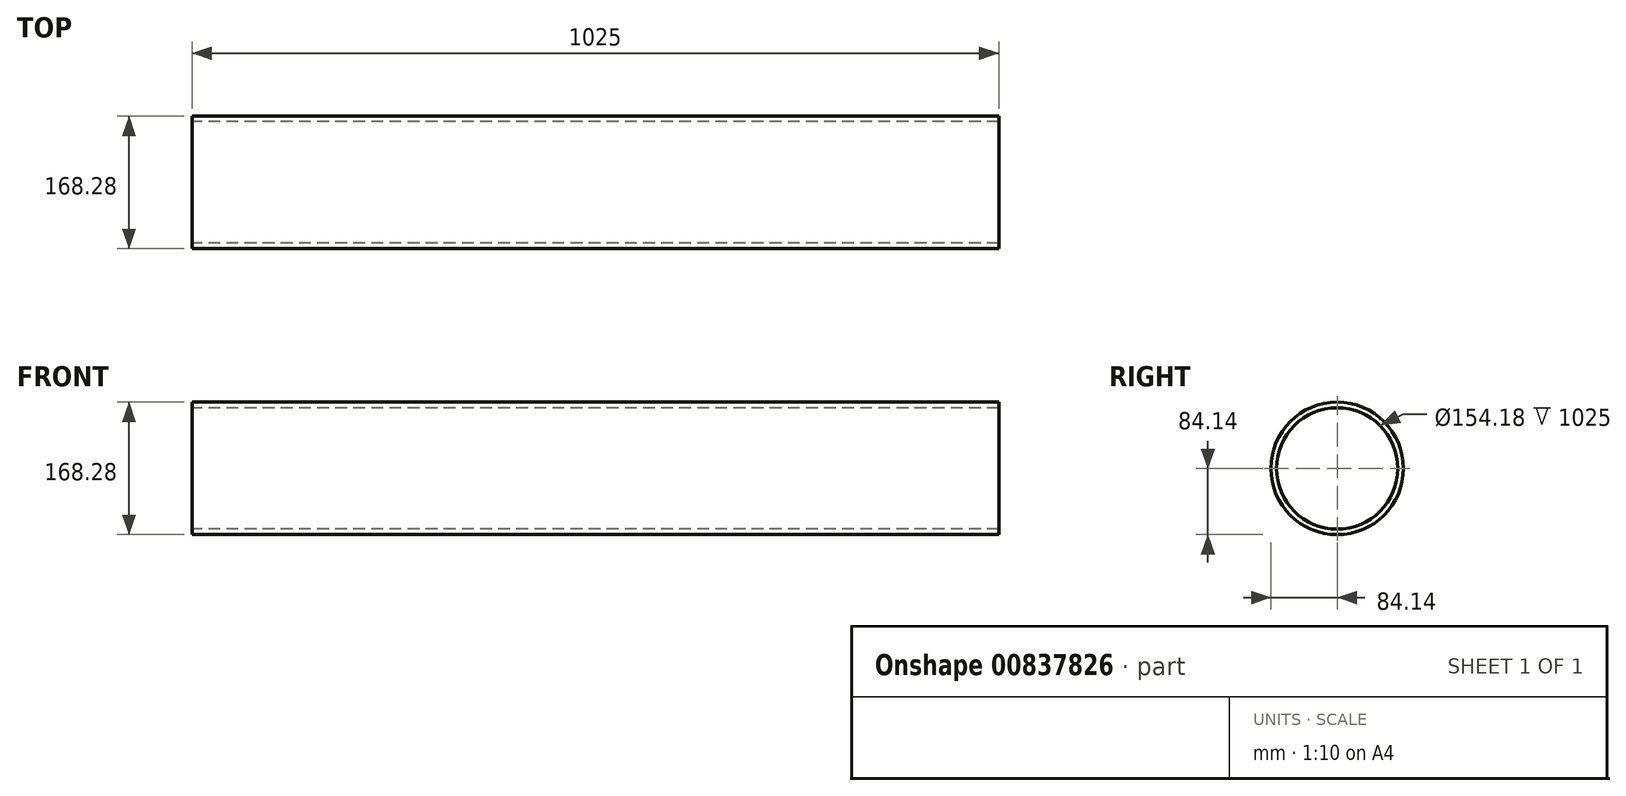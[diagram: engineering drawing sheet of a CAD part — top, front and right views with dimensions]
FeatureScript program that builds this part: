
annotation { "Feature Type Name" : "Feature", "Feature Type Description" : "" }
export const myFeature = defineFeature(function(context is Context, id is Id, definition is map)
    precondition{}
    {
        {
            var Q0;
            Q0=qCreatedBy(makeId("Right.planeOp"),FACE);
            var sketch = newSketch(context, id + "F0", { "sketchPlane" : qUnion([Q0])});
            skCircle(sketch, "E0", {"center": v(0, 0) * mm, "radius": 84.14 * mm});
            skCircle(sketch, "E1", {"center": v(0, 0) * mm, "radius": 77.09 * mm});
            skSolve(sketch);
        }
        {
            var Q0;
            Q0=makeQuery(id+"F0.imprint","IMPRINT",FACE,{"disambiguationData":[TD([[makeQuery(id+"F0.imprint","IMPRINT",EDGE,{"derivedFrom":sQuery(id+"F0.wireOp",EDGE,"E0")}),1.0]])]});
            extrude(context, id + "F1", {"entities" : qUnion([Q0]), "depth" : 1025 * mm, "offsetDistance" : 25.4 * mm});
        }
    });
